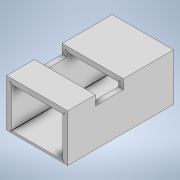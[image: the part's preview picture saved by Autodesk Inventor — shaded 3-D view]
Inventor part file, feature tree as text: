
AUTODESK INVENTOR PART (.ipt)
format: ipt  version: 2020 (Build 240168000, 168)  size: 259,584 bytes
history: native  units: in
note: dims shown in document units (in); Inventor stores cm internally (conversion verified against a paired STEP export)
features: extrude x9, sketch x9, projected_geometry x9
ambient origin geometry x8: Origin, YZ Plane, XZ Plane, XY Plane, X Axis, Y Axis, Z Axis, Center Point
bodies: Solid1 (feature_tree)
feature tree (27):
  extrude  "Extrusion1"  Depth=3.7402in
  extrude  "Extrusion2"  Depth=1.5748in
  extrude  "Extrusion3"  Depth=1.7717in
  extrude  "Extrusion4"  Depth=1.7717in
  extrude  "Extrusion5"  Depth=2.7559in TaperAngle=0.0deg
  extrude  "Extrusion6"  Depth=0.9843in TaperAngle=0.0deg
  extrude  "Extrusion7"  Depth=0.0984in TaperAngle=0.0deg
  extrude  "Extrusion9"  Depth=0.0197in
  extrude  "Extrusion10"  Depth=0.0197in
  sketch  "Sketch1"  dims[d0=1.9685in d1=3.7402in]
  sketch  "Sketch2"  dims[d2=1.5748in d3=0.0in d4=0.0984in]
  projected_geometry  "Projected Loop1"
  sketch  "Sketch3"  dims[d5=1.7717in d6=1.378in]
  projected_geometry  "Projected Loop2"
  sketch  "Sketch4"  dims[d7=3.5433in d8=0.0in d9=1.7717in]
  projected_geometry  "Projected Loop3"
  sketch  "Sketch5"  dims[d10=2.7559in d11=0.2362in d12=0.0in]
  projected_geometry  "Projected Loop4"
  sketch  "Sketch6"  dims[d13=0.9843in d14=0.2362in d15=0.0in]
  projected_geometry  "Projected Loop5"
  sketch  "Sketch7"  dims[d16=0.0984in d17=0.0in d18=0.0984in d19=0.0in]
  projected_geometry  "Projected Loop6"
  projected_geometry  "Projected Loop7"
  sketch  "Sketch10"  dims[d20=0.0984in d21=0.0in d29=0.0197in]
  projected_geometry  "Projected Loop9"
  sketch  "Sketch11"  dims[d30=0.0984in d31=0.0in d32=0.0197in d35=0.0197in d36=180.0deg d37=0.0787in d38=0.0197in d43=0.0591in d44=0.0197in d45=0.0984in d46=0.0in d47=0.0197in d48=0.0197in]
  projected_geometry  "Projected Loop10"
